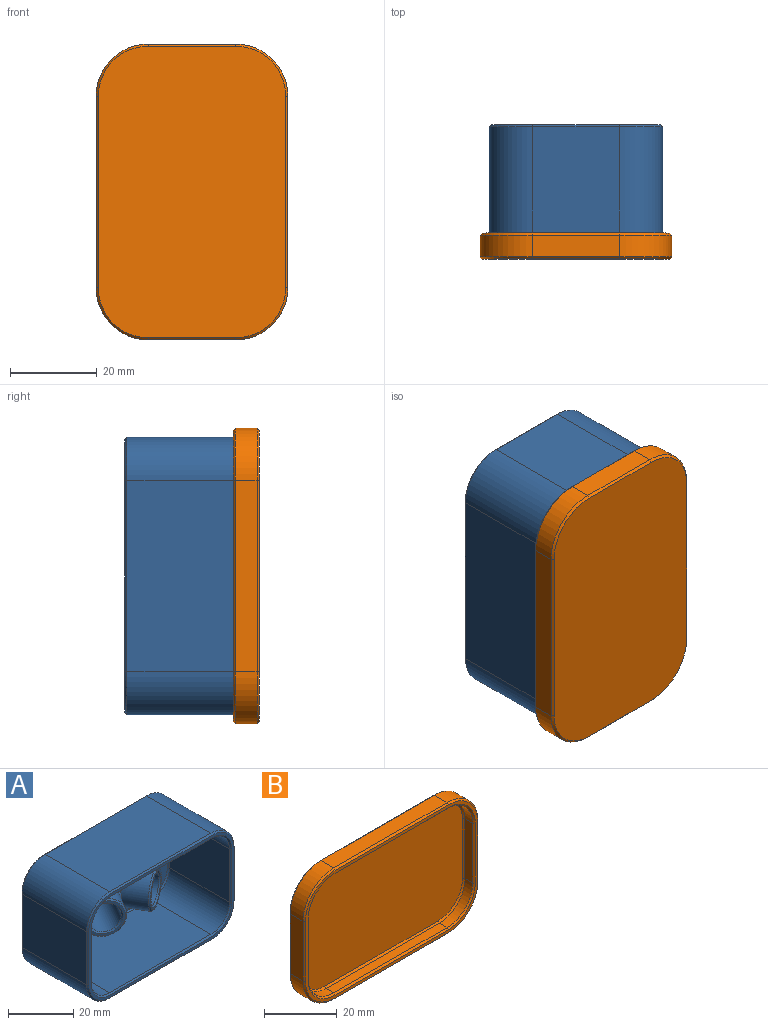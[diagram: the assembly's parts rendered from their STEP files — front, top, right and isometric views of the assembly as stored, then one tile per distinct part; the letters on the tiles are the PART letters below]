
ASSEMBLY  parts=2 mates=1
PART A: 67 faces, bbox 65.6x33.1x41.6 mm
  f0: plane 19.95x12.03mm, normal (0,-1,0), area 160.5mm2, adj f16,f25
  f1: plane 59.02x35.02mm, normal (0,-1,0), area 1712.2mm2, adj f26,f27,f35,f36,f37,f38,f39,f40
  f2: plane 44x28mm, normal (0,0,-1), area 1232mm2, adj f3,f17,f58,f66
  f3: cylinder r=10mm len=28mm, axis (0,1,0), area 439.8mm2, adj f2,f4,f57,f65
  f4: plane 28x20mm, normal (1,0,0), area 560mm2, adj f3,f5,f55,f63
  f5: cylinder r=10mm len=28mm, axis (0,1,0), area 439.8mm2, adj f4,f6,f53,f61
  f6: plane 44x28mm, normal (0,0,1), area 1232mm2, adj f5,f19,f51,f59
  f7: plane 63x39mm, normal (0,1,0), area 2379.5mm2, adj f59,f60,f61,f62,f63,f64,f65,f66
  f8: plane 44x26mm, normal (0,0,1), area 1144mm2, adj f12,f22,f35,f43
  f9: plane 44x26mm, normal (0,0,-1), area 1144mm2, adj f10,f20,f42,f50
  f10: cylinder r=8mm len=26mm, axis (0,1,0), area 326.7mm2, adj f9,f11,f40,f49
  f11: plane 26x20mm, normal (-1,0,0), area 520mm2, adj f10,f12,f38,f47
  f12: cylinder r=8mm len=26mm, axis (0,1,0), area 326.7mm2, adj f8,f11,f36,f45
  f13: plane 63x39mm, normal (0,-1,0), area 184.5mm2, adj f43,f44,f45,f46,f47,f48,f49,f50
  f14: plane 13x11.26mm, normal (0.5,-0.87,0), area 30.7mm2, adj f33,f34
  f15: cylinder r=7mm len=21.15mm, axis (0.5,-0.87,0), area 739.4mm2, adj f26,f30,f33
  f16: cylinder r=5.2mm len=19.72mm, axis (0.5,-0.87,0), area 456.8mm2, adj f0,f25,f34
  f17: cylinder r=10mm len=28mm, axis (0,1,0), area 439.8mm2, adj f2,f18,f56,f64
  f18: plane 28x20mm, normal (-1,0,0), area 560mm2, adj f17,f19,f54,f62
  f19: cylinder r=10mm len=28mm, axis (0,1,0), area 439.8mm2, adj f6,f18,f52,f60
  f20: cylinder r=8mm len=26mm, axis (0,1,0), area 326.7mm2, adj f9,f21,f41,f48
  f21: plane 26x20mm, normal (1,0,0), area 520mm2, adj f20,f22,f39,f46
  f22: cylinder r=8mm len=26mm, axis (0,1,0), area 326.7mm2, adj f8,f21,f37,f44
  f23: plane 13x11.26mm, normal (-0.5,-0.87,0), area 30.7mm2, adj f31,f32
  f24: cylinder r=7mm len=21.15mm, axis (-0.5,-0.87,0), area 551.8mm2, adj f27,f30,f31
  f25: cylinder r=5.2mm len=19.72mm, axis (-0.5,-0.87,0), area 467.7mm2, adj f0,f16,f32
  f26: bspline ~15.15x13.61mm, area 24.5mm2, adj f1,f15,f28,f29
  f27: bspline ~15x12.1mm, area 24.5mm2, adj f1,f24,f28,f29
  f28: plane 0.46x0.4mm, normal (0,-0.75,0.66), area 0.1mm2, adj f26,f27,f30
  f29: plane 0.46x0.4mm, normal (0,-0.75,-0.66), area 0.1mm2, adj f26,f27,f30
  f30: bspline ~12.85x8.88mm, area 15.2mm2, adj f15,f24,f28,f29
  f31: cone r=6.5mm half-angle=45deg, axis (0.5,0.87,0), area 30mm2, adj f23,f24
  f32: cone r=5.2mm half-angle=45deg, axis (-0.5,-0.87,0), area 24.2mm2, adj f23,f25
  f33: cone r=7mm half-angle=45deg, axis (-0.5,0.87,0), area 30mm2, adj f14,f15
  f34: cone r=5.7mm half-angle=45deg, axis (0.5,-0.87,0), area 24.2mm2, adj f14,f16
  f35: plane 44x0.5mm, normal (0,-0.71,0.71), area 31.1mm2, adj f1,f8,f36,f37
  f36: cone r=8mm half-angle=45deg, axis (0,-1,0), area 8.6mm2, adj f1,f12,f35,f38
  f37: cone r=7.5mm half-angle=45deg, axis (0,-1,0), area 8.6mm2, adj f1,f22,f35,f39
  f38: plane 20x0.5mm, normal (-0.71,-0.71,0), area 14.1mm2, adj f1,f11,f36,f40
  f39: plane 20x0.5mm, normal (0.71,-0.71,0), area 14.1mm2, adj f1,f21,f37,f41
  f40: cone r=8mm half-angle=45deg, axis (0,-1,0), area 8.6mm2, adj f1,f10,f38,f42
  f41: cone r=7.5mm half-angle=45deg, axis (0,-1,0), area 8.6mm2, adj f1,f20,f39,f42
  f42: plane 44x0.5mm, normal (0,-0.71,-0.71), area 31.1mm2, adj f1,f9,f40,f41
  f43: plane 44x0.5mm, normal (0,-0.71,0.71), area 31.1mm2, adj f8,f13,f44,f45
  f44: cone r=8.5mm half-angle=45deg, axis (0,-1,0), area 9.2mm2, adj f13,f22,f43,f46
  f45: cone r=8mm half-angle=45deg, axis (0,-1,0), area 9.2mm2, adj f12,f13,f43,f47
  f46: plane 20x0.5mm, normal (0.71,-0.71,0), area 14.1mm2, adj f13,f21,f44,f48
  f47: plane 20x0.5mm, normal (-0.71,-0.71,0), area 14.1mm2, adj f11,f13,f45,f49
  f48: cone r=8.5mm half-angle=45deg, axis (0,-1,0), area 9.2mm2, adj f13,f20,f46,f50
  f49: cone r=8mm half-angle=45deg, axis (0,-1,0), area 9.2mm2, adj f10,f13,f47,f50
  f50: plane 44x0.5mm, normal (0,-0.71,-0.71), area 31.1mm2, adj f9,f13,f48,f49
  f51: plane 44x0.5mm, normal (0,-0.71,0.71), area 31.1mm2, adj f6,f13,f52,f53
  f52: cone r=10mm half-angle=45deg, axis (0,1,0), area 10.8mm2, adj f13,f19,f51,f54
  f53: cone r=9.5mm half-angle=45deg, axis (0,1,0), area 10.8mm2, adj f5,f13,f51,f55
  f54: plane 20x0.5mm, normal (-0.71,-0.71,0), area 14.1mm2, adj f13,f18,f52,f56
  f55: plane 20x0.5mm, normal (0.71,-0.71,0), area 14.1mm2, adj f4,f13,f53,f57
  f56: cone r=10mm half-angle=45deg, axis (0,1,0), area 10.8mm2, adj f13,f17,f54,f58
  f57: cone r=9.5mm half-angle=45deg, axis (0,1,0), area 10.8mm2, adj f3,f13,f55,f58
  f58: plane 44x0.5mm, normal (0,-0.71,-0.71), area 31.1mm2, adj f2,f13,f56,f57
  f59: plane 44x0.5mm, normal (0,0.71,0.71), area 31.1mm2, adj f6,f7,f60,f61
  f60: cone r=9.5mm half-angle=45deg, axis (0,-1,0), area 10.8mm2, adj f7,f19,f59,f62
  f61: cone r=10mm half-angle=45deg, axis (0,-1,0), area 10.8mm2, adj f5,f7,f59,f63
  f62: plane 20x0.5mm, normal (-0.71,0.71,0), area 14.1mm2, adj f7,f18,f60,f64
  f63: plane 20x0.5mm, normal (0.71,0.71,0), area 14.1mm2, adj f4,f7,f61,f65
  f64: cone r=9.5mm half-angle=45deg, axis (0,-1,0), area 10.8mm2, adj f7,f17,f62,f66
  f65: cone r=10mm half-angle=45deg, axis (0,-1,0), area 10.8mm2, adj f3,f7,f63,f66
  f66: plane 44x0.5mm, normal (0,0.71,-0.71), area 31.1mm2, adj f2,f7,f64,f65
PART B: 51 faces, bbox 68.2x6x44.2 mm
  f0: plane 20.2x5mm, normal (1,0,0), area 101mm2, adj f1,f7,f23,f39
  f1: cylinder r=12mm len=12mm, axis (0,1,0), area 94.2mm2, adj f0,f2,f25,f41
  f2: plane 44.2x5mm, normal (0,0,1), area 221mm2, adj f1,f3,f26,f42
  f3: cylinder r=12mm len=12mm, axis (0,1,0), area 94.2mm2, adj f2,f4,f24,f40
  f4: plane 20.2x5mm, normal (-1,0,0), area 101mm2, adj f3,f5,f22,f38
  f5: cylinder r=12mm len=12mm, axis (0,1,0), area 94.2mm2, adj f4,f6,f20,f36
  f6: plane 44.2x5mm, normal (0,0,-1), area 221mm2, adj f5,f7,f19,f35
  f7: cylinder r=12mm len=12mm, axis (0,1,0), area 94.2mm2, adj f0,f6,f21,f37
  f8: plane 67.2x43.2mm, normal (0,1,0), area 2789.5mm2, adj f35,f36,f37,f38,f39,f40,f41,f42
  f9: cylinder r=10mm len=10mm, axis (0,1,0), area 47.1mm2, adj f10,f16,f27,f43
  f10: plane 44.2x3mm, normal (0,0,1), area 132.6mm2, adj f9,f11,f29,f44
  f11: cylinder r=10mm len=10mm, axis (0,1,0), area 47.1mm2, adj f10,f12,f31,f46
  f12: plane 20.2x3mm, normal (1,0,0), area 60.6mm2, adj f11,f13,f33,f48
  f13: cylinder r=10mm len=10mm, axis (0,1,0), area 47.1mm2, adj f12,f14,f34,f50
  f14: plane 44.2x3mm, normal (0,0,-1), area 132.6mm2, adj f13,f15,f32,f49
  f15: cylinder r=10mm len=10mm, axis (0,1,0), area 47.1mm2, adj f14,f16,f30,f47
  f16: plane 20.2x3mm, normal (-1,0,0), area 60.6mm2, adj f9,f15,f28,f45
  f17: plane 67.2x43.2mm, normal (0,-1,0), area 197.9mm2, adj f19,f20,f21,f22,f23,f24,f25,f26
  f18: plane 63.2x39.2mm, normal (0,-1,0), area 2400mm2, adj f43,f44,f45,f46,f47,f48,f49,f50
  f19: plane 44.2x0.5mm, normal (0,-0.71,-0.71), area 31.3mm2, adj f6,f17,f20,f21
  f20: cone r=11.5mm half-angle=45deg, axis (0,1,0), area 13.1mm2, adj f5,f17,f19,f22
  f21: cone r=11.5mm half-angle=45deg, axis (0,1,0), area 13.1mm2, adj f7,f17,f19,f23
  f22: plane 20.2x0.5mm, normal (-0.71,-0.71,0), area 14.3mm2, adj f4,f17,f20,f24
  f23: plane 20.2x0.5mm, normal (0.71,-0.71,0), area 14.3mm2, adj f0,f17,f21,f25
  f24: cone r=11.5mm half-angle=45deg, axis (0,1,0), area 13.1mm2, adj f3,f17,f22,f26
  f25: cone r=11.5mm half-angle=45deg, axis (0,1,0), area 13.1mm2, adj f1,f17,f23,f26
  f26: plane 44.2x0.5mm, normal (0,-0.71,0.71), area 31.3mm2, adj f2,f17,f24,f25
  f27: cone r=10mm half-angle=45deg, axis (0,-1,0), area 11.4mm2, adj f9,f17,f28,f29
  f28: plane 20.2x0.5mm, normal (-0.71,-0.71,0), area 14.3mm2, adj f16,f17,f27,f30
  f29: plane 44.2x0.5mm, normal (0,-0.71,0.71), area 31.3mm2, adj f10,f17,f27,f31
  f30: cone r=10mm half-angle=45deg, axis (0,-1,0), area 11.4mm2, adj f15,f17,f28,f32
  f31: cone r=10mm half-angle=45deg, axis (0,-1,0), area 11.4mm2, adj f11,f17,f29,f33
  f32: plane 44.2x0.5mm, normal (0,-0.71,-0.71), area 31.3mm2, adj f14,f17,f30,f34
  f33: plane 20.2x0.5mm, normal (0.71,-0.71,0), area 14.3mm2, adj f12,f17,f31,f34
  f34: cone r=10mm half-angle=45deg, axis (0,-1,0), area 11.4mm2, adj f13,f17,f32,f33
  f35: plane 44.2x0.5mm, normal (0,0.71,-0.71), area 31.3mm2, adj f6,f8,f36,f37
  f36: cone r=12mm half-angle=45deg, axis (0,-1,0), area 13.1mm2, adj f5,f8,f35,f38
  f37: cone r=12mm half-angle=45deg, axis (0,-1,0), area 13.1mm2, adj f7,f8,f35,f39
  f38: plane 20.2x0.5mm, normal (-0.71,0.71,0), area 14.3mm2, adj f4,f8,f36,f40
  f39: plane 20.2x0.5mm, normal (0.71,0.71,0), area 14.3mm2, adj f0,f8,f37,f41
  f40: cone r=12mm half-angle=45deg, axis (0,-1,0), area 13.1mm2, adj f3,f8,f38,f42
  f41: cone r=12mm half-angle=45deg, axis (0,-1,0), area 13.1mm2, adj f1,f8,f39,f42
  f42: plane 44.2x0.5mm, normal (0,0.71,0.71), area 31.3mm2, adj f2,f8,f40,f41
  f43: cone r=10mm half-angle=45deg, axis (0,-1,0), area 10.8mm2, adj f9,f18,f44,f45
  f44: plane 44.2x0.5mm, normal (0,-0.71,0.71), area 31.3mm2, adj f10,f18,f43,f46
  f45: plane 20.2x0.5mm, normal (-0.71,-0.71,0), area 14.3mm2, adj f16,f18,f43,f47
  f46: cone r=10mm half-angle=45deg, axis (0,-1,0), area 10.8mm2, adj f11,f18,f44,f48
  f47: cone r=10mm half-angle=45deg, axis (0,-1,0), area 10.8mm2, adj f15,f18,f45,f49
  f48: plane 20.2x0.5mm, normal (0.71,-0.71,0), area 14.3mm2, adj f12,f18,f46,f50
  f49: plane 44.2x0.5mm, normal (0,-0.71,-0.71), area 31.3mm2, adj f14,f18,f47,f50
  f50: cone r=10mm half-angle=45deg, axis (0,-1,0), area 10.8mm2, adj f13,f18,f48,f49
PLACE A rot(axis=(-0.71,0,0.71),180deg) t=(29.81,-36.13,-32.59)mm
PLACE B rot(axis=(0.71,0,0.71),180deg) t=(79.23,-38.13,19.62)mm
MATE slider B.f18 <-> A.f7  axis (0,1,0) through (27.81,-36.13,-32.59)mm
